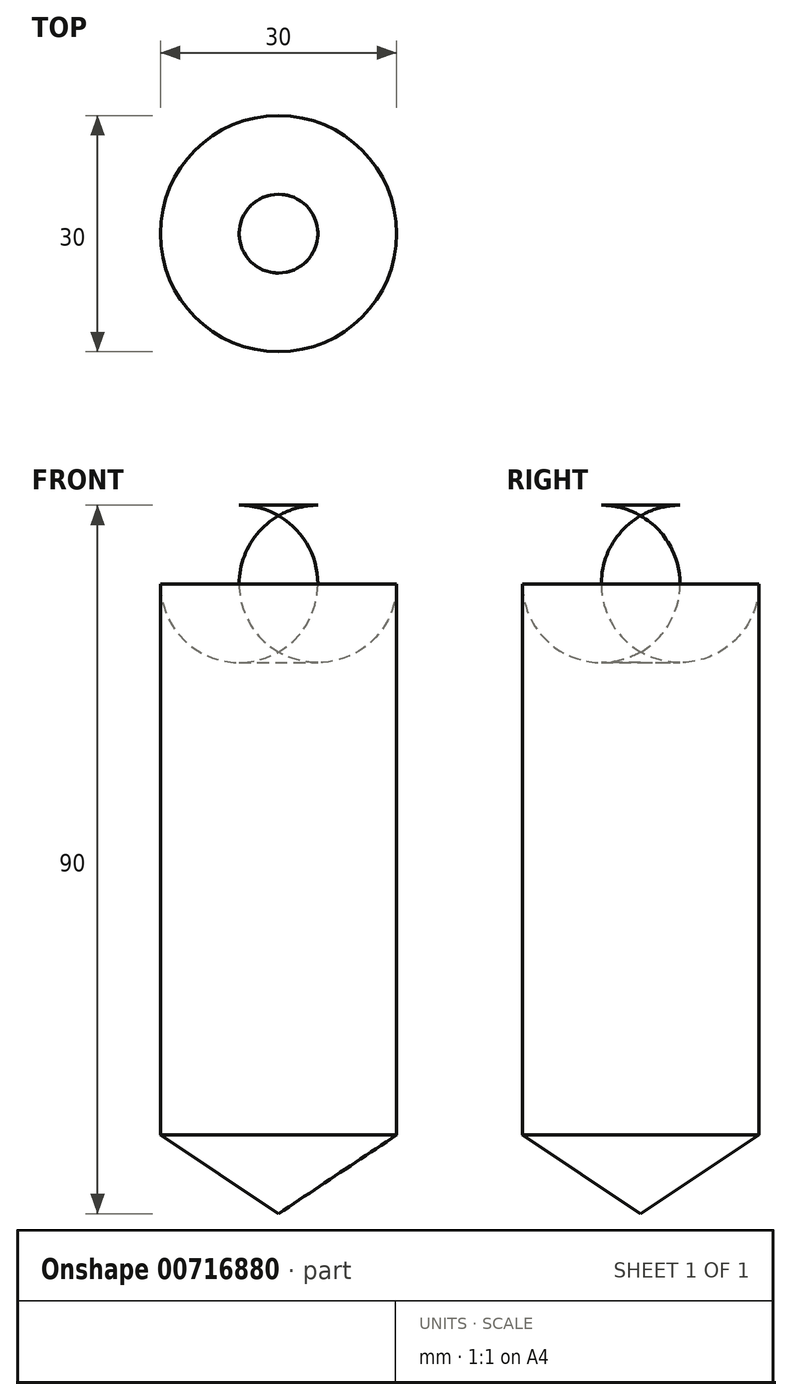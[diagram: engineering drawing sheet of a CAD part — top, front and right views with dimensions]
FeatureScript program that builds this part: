
annotation { "Feature Type Name" : "Feature", "Feature Type Description" : "" }
export const myFeature = defineFeature(function(context is Context, id is Id, definition is map)
    precondition{}
    {
        {
            var Q0;
            Q0=qCreatedBy(makeId("Front.planeOp"),FACE);
            var sketch = newSketch(context, id + "F0", { "sketchPlane" : qUnion([Q0])});
            skLineSegment(sketch, "E0", {"start": v(-15, 39.65) * mm, "end": v(0, 39.65) * mm});
            skLineSegment(sketch, "E1", {"start": v(0, -50.35) * mm, "end": v(-15, -40.35) * mm});
            skPoint(sketch, "E2.start.orphan", {"position": v(-15, -0.35) * mm});
            skLineSegment(sketch, "E3", {"start": v(-15, 39.65) * mm, "end": v(-15, -40.35) * mm});
            skLineSegment(sketch, "E4", {"start": v(0, 39.65) * mm, "end": v(0, -50.35) * mm});
            skSolve(sketch);
        }
        {
            var Q0;
            Q0=makeQuery(id+"F0.imprint","IMPRINT",FACE,{"disambiguationData":[TD([[makeQuery(id+"F0.imprint","IMPRINT",EDGE,{"derivedFrom":sQuery(id+"F0.wireOp",EDGE,"E0")}),-1.0]])]});
            var Q1;
            Q1=sQuery(id+"F0.wireOp",EDGE,"E4");
            revolve(context, id + "F1", {"surfaceOperationType" : NewSurfaceOperationType.NEW, "entities" : qUnion([Q0]), "axis" : qUnion([Q1]), "revolveType" : RevolveType.FULL});
        }
        {
            var Q0;
            Q0=makeQuery(id+"F1.opRevolve","SWEPT_EDGE",EDGE,{"disambiguationData":[OSD([sQuery(id+"F0.wireOp",EDGE,"E0"),sQuery(id+"F0.wireOp",EDGE,"E3")])]});
            fillet(context, id + "F2", {"entities" : qUnion([Q0]), "radius" : 10 * mm, "tangentPropagation" : true, "allowEdgeOverflow" : false});
        }
    });
